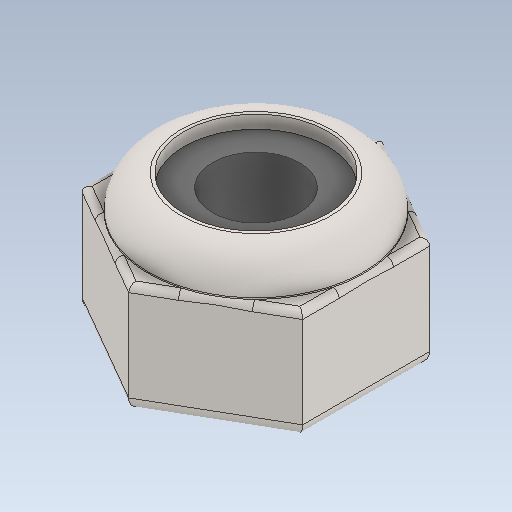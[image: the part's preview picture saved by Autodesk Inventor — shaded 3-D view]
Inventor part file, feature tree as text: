
AUTODESK INVENTOR PART (.ipt)
format: ipt  version: 2020 (Build 240168000, 168)  size: 215,040 bytes
history: native  units: in
note: dims shown in document units (in); Inventor stores cm internally (conversion verified against a paired STEP export)
features: fillet x1
ambient origin geometry x8: Origin, YZ Plane, XZ Plane, XY Plane, X Axis, Y Axis, Z Axis, Center Point
bodies: Solid1 (feature_tree)
feature tree (1):
  fillet  "Fillet6"  [1 undecoded]
note: 1 required parameter value undecoded (feature->parameter linkage not recoverable at this tier; creation-order binding heuristic only, values carry confidence <= 0.55)
